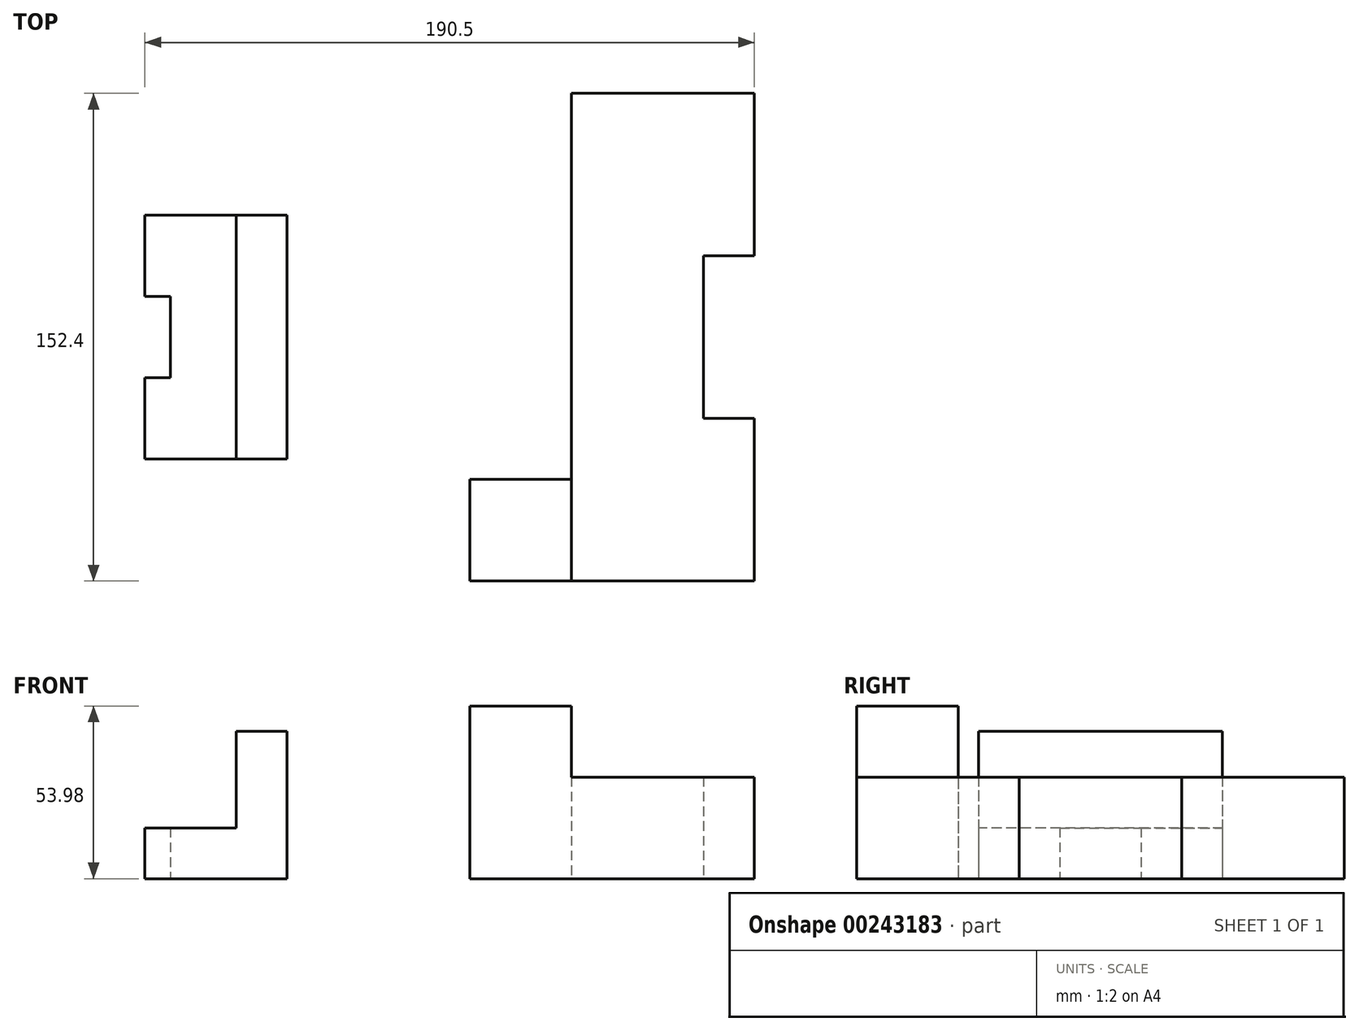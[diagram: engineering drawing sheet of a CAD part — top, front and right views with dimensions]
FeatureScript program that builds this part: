
annotation { "Feature Type Name" : "Feature", "Feature Type Description" : "" }
export const myFeature = defineFeature(function(context is Context, id is Id, definition is map)
    precondition{}
    {
        {
            var Q0;
            Q0=qCreatedBy(makeId("Top.planeOp"),FACE);
            var sketch = newSketch(context, id + "F0", { "sketchPlane" : qUnion([Q0])});
            skLineSegment(sketch, "E0", {"start": v(-127, -25.4) * mm, "end": v(-127, -76.2) * mm});
            skLineSegment(sketch, "E1", {"start": v(-127, -76.2) * mm, "end": v(127, -76.2) * mm});
            skLineSegment(sketch, "E2", {"start": v(-127, -25.4) * mm, "end": v(-111.12, -25.4) * mm});
            skLineSegment(sketch, "E3", {"start": v(-111.12, -25.4) * mm, "end": v(-111.12, 25.4) * mm});
            skLineSegment(sketch, "E4", {"start": v(-111.12, 25.4) * mm, "end": v(-127, 25.4) * mm});
            skLineSegment(sketch, "E5", {"start": v(-127, 25.4) * mm, "end": v(-127, 76.2) * mm});
            skLineSegment(sketch, "E6", {"start": v(-127, 76.2) * mm, "end": v(127, 76.2) * mm});
            skLineSegment(sketch, "E7", {"start": v(127, -76.2) * mm, "end": v(127, -25.4) * mm});
            skLineSegment(sketch, "E8", {"start": v(127, 76.2) * mm, "end": v(127, 25.4) * mm});
            skLineSegment(sketch, "E9", {"start": v(127, -25.4) * mm, "end": v(111.12, -25.4) * mm});
            skLineSegment(sketch, "E10", {"start": v(127, 25.4) * mm, "end": v(111.12, 25.4) * mm});
            skLineSegment(sketch, "E11", {"start": v(111.12, 25.4) * mm, "end": v(111.12, -25.4) * mm});
            skLineSegment(sketch, "E12", {"start": v(127, 76.2) * mm, "end": v(69.85, 76.2) * mm});
            skLineSegment(sketch, "E13", {"start": v(-127, 76.2) * mm, "end": v(-69.85, 76.2) * mm});
            skLineSegment(sketch, "E14", {"start": v(-127, -76.2) * mm, "end": v(-69.85, -76.2) * mm});
            skLineSegment(sketch, "E15", {"start": v(127, -76.2) * mm, "end": v(69.85, -76.2) * mm});
            skLineSegment(sketch, "E16", {"start": v(-69.85, 76.2) * mm, "end": v(-69.85, -76.2) * mm});
            skLineSegment(sketch, "E17", {"start": v(69.85, 76.2) * mm, "end": v(69.85, -76.2) * mm});
            skLineSegment(sketch, "E18", {"start": v(-69.85, -76.2) * mm, "end": v(-38.1, -76.2) * mm});
            skLineSegment(sketch, "E19", {"start": v(-38.1, -76.2) * mm, "end": v(-38.1, 76.2) * mm});
            skLineSegment(sketch, "E20", {"start": v(69.85, -76.2) * mm, "end": v(38.1, -76.2) * mm});
            skLineSegment(sketch, "E21", {"start": v(38.1, -76.2) * mm, "end": v(38.1, 76.2) * mm});
            skLineSegment(sketch, "E22", {"start": v(-38.1, 76.2) * mm, "end": v(-38.1, 44.45) * mm});
            skLineSegment(sketch, "E23", {"start": v(-38.1, 44.45) * mm, "end": v(-69.85, 44.45) * mm});
            skLineSegment(sketch, "E24", {"start": v(-38.1, 44.45) * mm, "end": v(-38.1, -44.45) * mm});
            skLineSegment(sketch, "E25", {"start": v(-38.1, -44.45) * mm, "end": v(-69.85, -44.45) * mm});
            skLineSegment(sketch, "E26", {"start": v(69.85, 76.2) * mm, "end": v(69.85, 44.45) * mm});
            skLineSegment(sketch, "E27", {"start": v(69.85, 44.45) * mm, "end": v(69.85, -44.45) * mm});
            skLineSegment(sketch, "E28", {"start": v(69.85, 44.45) * mm, "end": v(38.1, 44.45) * mm});
            skLineSegment(sketch, "E29", {"start": v(69.85, -44.45) * mm, "end": v(38.1, -44.45) * mm});
            skCircle(sketch, "E30", {"center": v(0, 0) * mm, "radius": 15.88 * mm});
            skLineSegment(sketch, "E31", {"start": v(-127, -76.2) * mm, "end": v(0, -76.2) * mm});
            skSolve(sketch);
        }
        {
            var Q0;
            Q0=makeQuery(id+"F0.imprint","IMPRINT",FACE,{"disambiguationData":[TD([[makeQuery(id+"F0.imprint","IMPRINT",EDGE,{"derivedFrom":sQuery(id+"F0.wireOp",EDGE,"E7")}),1.0]])]});
            var Q1;
            Q1=makeQuery(id+"F0.imprint","IMPRINT",FACE,{"disambiguationData":[TD([[makeQuery(id+"F0.imprint","IMPRINT",EDGE,{"derivedFrom":sQuery(id+"F0.wireOp",EDGE,"E0")}),1.0]])]});
            var Q2;
            Q2=sQuery(id+"F0.wireOp",EDGE,"E2");
            var Q3;
            Q3=sQuery(id+"F0.wireOp",EDGE,"E0");
            var Q4;
            Q4=sQuery(id+"F0.wireOp",EDGE,"E1");
            var Q5;
            Q5=sQuery(id+"F0.wireOp",EDGE,"E7");
            var Q6;
            Q6=sQuery(id+"F0.wireOp",EDGE,"E11");
            var Q7;
            Q7=sQuery(id+"F0.wireOp",EDGE,"E8");
            var Q8;
            Q8=sQuery(id+"F0.wireOp",EDGE,"E10");
            var Q9;
            Q9=sQuery(id+"F0.wireOp",EDGE,"E9");
            var Q10;
            Q10=sQuery(id+"F0.wireOp",EDGE,"E12");
            var Q11;
            Q11=sQuery(id+"F0.wireOp",EDGE,"E6");
            var Q12;
            Q12=sQuery(id+"F0.wireOp",EDGE,"E5");
            var Q13;
            Q13=sQuery(id+"F0.wireOp",EDGE,"E3");
            var Q14;
            Q14=sQuery(id+"F0.wireOp",EDGE,"E4");
            extrude(context, id + "F1", {"entities" : qUnion([Q0, Q1]), "surfaceEntities" : qUnion([Q2, Q3, Q4, Q5, Q6, Q7, Q8, Q9, Q10, Q11, Q12, Q13, Q14]), "depth" : 31.75 * mm});
        }
        {
            var Q0;
            {var subQ3=sQuery(id+"F0.wireOp",EDGE,"E22");Q0=makeQuery(id+"F0.imprint","IMPRINT",FACE,{"disambiguationData":[TD([[makeQuery(id+"F0.imprint","IMPRINT",EDGE,{"derivedFrom":subQ3}),-1.0]])]});}
            var Q1;
            {var subQ0=sQuery(id+"F0.wireOp",EDGE,"E26");Q1=makeQuery(id+"F0.imprint","IMPRINT",FACE,{"disambiguationData":[TD([[makeQuery(id+"F0.imprint","IMPRINT",EDGE,{"derivedFrom":subQ0}),-1.0]])]});}
            var Q2;
            {var subQ0=sQuery(id+"F0.wireOp",EDGE,"E18");Q2=makeQuery(id+"F0.imprint","IMPRINT",FACE,{"disambiguationData":[TD([[makeQuery(id+"F0.imprint","IMPRINT",EDGE,{"derivedFrom":subQ0}),1.0]])]});}
            var Q3;
            {var subQ0=sQuery(id+"F0.wireOp",EDGE,"E20");Q3=makeQuery(id+"F0.imprint","IMPRINT",FACE,{"disambiguationData":[TD([[makeQuery(id+"F0.imprint","IMPRINT",EDGE,{"derivedFrom":subQ0}),-1.0]])]});}
            var Q4;
            {var subQ4=sQuery(id+"F0.wireOp",EDGE,"E19");Q4=makeQuery(id+"F0.imprint","IMPRINT",FACE,{"disambiguationData":[TD([[makeQuery(id+"F0.imprint","IMPRINT",EDGE,{"derivedFrom":subQ4}),1.0]])]});}
            extrude(context, id + "F2", {"entities" : qUnion([Q0, Q1, Q2, Q3, Q4]), "operationType" : NewBodyOperationType.ADD, "depth" : 92.07 * mm});
        }
        {
            var Q0;
            {var subQ1=sQuery(id+"F0.wireOp",EDGE,"E1");Q0=makeQuery(id+"F0.imprint","IMPRINT",FACE,{"disambiguationData":[TD([[makeQuery(id+"F0.imprint","IMPRINT",EDGE,{"derivedFrom":subQ1}),1.0]])]});}
            extrude(context, id + "F3", {"entities" : qUnion([Q0]), "operationType" : NewBodyOperationType.ADD, "depth" : 53.97 * mm});
        }
        {
            var Q0;
            Q0=makeQuery(id+"F0.imprint","IMPRINT",FACE,{"disambiguationData":[TD([[makeQuery(id+"F0.imprint","IMPRINT",EDGE,{"derivedFrom":sQuery(id+"F0.wireOp",EDGE,"E27")}),-1.0]])]});
            var Q1;
            {var subQ0=sQuery(id+"F0.wireOp",EDGE,"E23");Q1=makeQuery(id+"F0.imprint","IMPRINT",FACE,{"disambiguationData":[TD([[makeQuery(id+"F0.imprint","IMPRINT",EDGE,{"derivedFrom":subQ0}),1.0]])]});}
            extrude(context, id + "F4", {"entities" : qUnion([Q0, Q1]), "operationType" : NewBodyOperationType.ADD, "depth" : 73.02 * mm});
        }
        {
            var Q0;
            Q0=makeQuery(id+"F1.opExtrude","SWEPT_BODY",BODY,{"disambiguationData":[OSD([sQuery(id+"F0.wireOp",EDGE,"E0"),sQuery(id+"F0.wireOp",EDGE,"E2"),sQuery(id+"F0.wireOp",EDGE,"E3"),sQuery(id+"F0.wireOp",EDGE,"E4"),sQuery(id+"F0.wireOp",EDGE,"E5"),sQuery(id+"F0.wireOp",EDGE,"E13"),sQuery(id+"F0.wireOp",EDGE,"E16"),sQuery(id+"F0.wireOp",EDGE,"E31")])]});
            var Q1;
            Q1=qCreatedBy(makeId("Origin.pointOp"),VERTEX);
            transform(context, id + "F5", {"entities" : qUnion([Q0]), "transformType" : TransformType.SCALE_UNIFORMLY, "scale" : .5, "scalePoint" : qUnion([Q1]), "makeCopy" : false});
        }
    });
